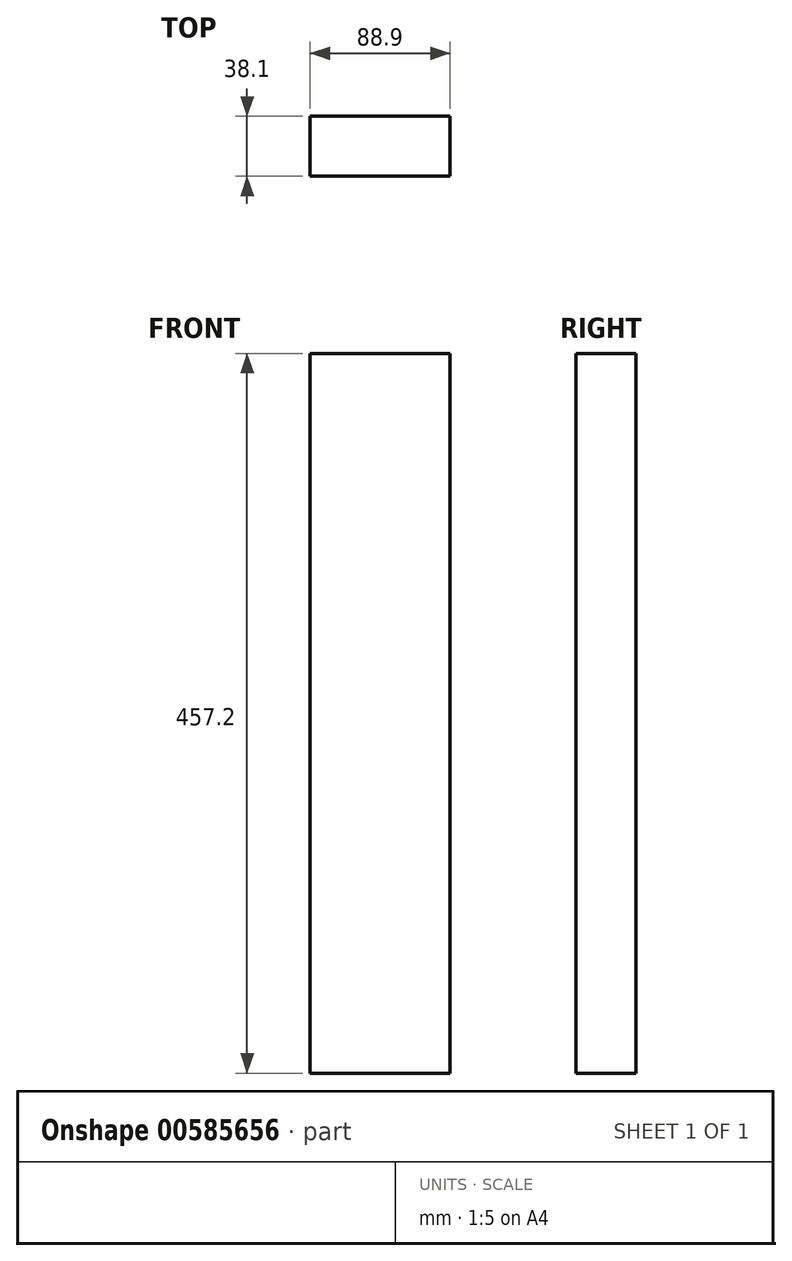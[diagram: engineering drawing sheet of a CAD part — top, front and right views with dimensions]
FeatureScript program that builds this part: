
annotation { "Feature Type Name" : "Feature", "Feature Type Description" : "" }
export const myFeature = defineFeature(function(context is Context, id is Id, definition is map)
    precondition{}
    {
        {
            var Q0;
            Q0=qCreatedBy(makeId("Front.planeOp"),FACE);
            var sketch = newSketch(context, id + "F0", { "sketchPlane" : qUnion([Q0])});
            skLineSegment(sketch, "E0", {"start": v(0, 0) * mm, "end": v(88.9, 0) * mm});
            skLineSegment(sketch, "E1", {"start": v(88.9, 0) * mm, "end": v(88.9, 457.2) * mm});
            skLineSegment(sketch, "E2", {"start": v(0, 457.2) * mm, "end": v(0, 0) * mm});
            skLineSegment(sketch, "E3", {"start": v(0, 457.2) * mm, "end": v(88.9, 457.2) * mm});
            skPoint(sketch, "E4.orphan", {"position": v(0, 1060.45) * mm});
            skSolve(sketch);
        }
        {
            var Q0;
            Q0=makeQuery(id+"F0.imprint","IMPRINT",FACE,{"disambiguationData":[TD([[makeQuery(id+"F0.imprint","IMPRINT",EDGE,{"derivedFrom":sQuery(id+"F0.wireOp",EDGE,"E0")}),1.0]])]});
            var Q1;
            Q1=qConstructionFilter(qBodyType(qCreatedBy(id+"F0",EDGE),BodyType.WIRE),ConstructionObject.NO);
            extrude(context, id + "F1", {"entities" : qUnion([Q0]), "surfaceEntities" : qUnion([Q1]), "oppositeDirection" : true, "depth" : 38.1 * mm, "offsetDistance" : 25.4 * mm});
        }
    });
